# Revit family: IS_Concept_Multiproduct_BIM_GB_E0321;E0322;E0323;E0324
name_source: partatom
category: Casework
revit_build: Autodesk Revit 2015 (Build: 20140606_1530(x64)
units: mm (PartAtom-declared; Revit-internal decimal feet)

## types (8) — shared parameters
2Doors = Yes
Accessories = www.idealspec.co.uk
AreaUnits = millimeters
Assembly Code = C1030200
AssetType = Fixed
BREEAM = No
Brand = Ideal Standard
CodePerformance = FSC
ConnectionType = Plumbing
Default Elevation = 2000 mm  [stored 6.56168 ft]
DurationUnit = year
ECA = No
ExpectedLife = 30
IfcExportAs = IfcFurnitureType
IfcExportType = Bathroom cabinets
InstallationInstructions = www.idealspec.co.uk/resources.html
LinearUnits = millimeters
Manufacturer = Ideal Standard (UK) Ltd
ManufacturerURL = www.idealspec.co.uk
MetalMtl = ISI_IdealStandard_Furniture_Metal_Chrome_Render
MirrorMtl = ISI_IdealStandard_Furniture_Mirror_Render
NBSDescription = Bathroom integrated furniture
NBSReference = 45-35-72/320
NominalDepth = 170 mm  [stored 0.557743 ft]
NominalHeight = 700 mm  [stored 2.29659 ft]
NominalLength = 170 mm  [stored 0.557743 ft]
Shape = Rectangular
Space = Internal
SpareParts = www.fastpart-spares.co.uk
TMV3 = No
URL = www.idealspec.co.uk
Uniclass2 = Pr_40_30_78_03
Uniclass2015Code = Pr_40_30_78_03
Uniclass2015Description = Bathroom cabinets
Uniclass2015Reference = Pr_40_30_78_03
Uniclass2015Title = Bathroom cabinets
Uniclass2015Version = Products v1.1
Version = 1
VolumeUnits = Litres
WRAS = No
WarrantyDescription = Manufacturers Warranty
WarrantyDurationParts = 5
WarrantyDurationUnit = year
WaterEfficientProduct = No
zero-valued in all types: Cost

## per-type parameters (varying)
| type | BIMObjectName | BarCode | Color | Description | DoorC1 | DoorC2 | DoorD | Features | Finish | LaminateMtl | Model | ModelNumber | ModelReference | Name | NettWeight | NominalWidth | ProductInformation | Size |
| E0336KP - Concept Space 1300 mm Mirror cabinet - Inox | ISI_IdealStandard_Furniture_ConceptSpace_E0336KP | 5017830452188 | Aluminium Effect | Concept Space 1300 mm mirror cabinet, Aluminium Effect | 398 mm  [stored 1.30577 ft] | 398 mm  [stored 1.30577 ft] | 498 mm  [stored 1.63386 ft] | 1300 mm mirror cabinet, Aluminium Effect | Aluminium Effect | ISI_IdealStandard_Furniture_Metal_Aluminium_KP_Render | E0324KP | E0324KP | Concept Space 1300 mm mirror cabinet, Aluminium Effect | Furniture_ConceptSpace_E0336KP_IdealStandard | 36 Kg | 1300 mm  [stored 4.26509 ft] | www.idealspec.co.uk/assets/datasheet/E0336KP | 700 x 170 x 1300 mm |
| E0335KP - Concept Space 1000 mm Mirror cabinet - Inox | ISI_IdealStandard_Furniture_ConceptSpace_E0335KP | 5017830452164 | Aluminium Effect | Concept Space 1000 mm mirror cabinet, Aluminium Effect | 298 mm  [stored 0.97769 ft] | 298 mm  [stored 0.97769 ft] | 398 mm  [stored 1.30577 ft] | 1000 mm mirror cabinet, Aluminium Effect | Aluminium Effect | ISI_IdealStandard_Furniture_Metal_Aluminium_KP_Render | E0323KP | E0323KP | Concept Space 1000 mm mirror cabinet, Aluminium Effect | Furniture_ConceptSpace_E0335KP_IdealStandard | 30 Kg | 1000 mm  [stored 3.28084 ft] | www.idealspec.co.uk/assets/datasheet/E0335KP | 700 x 170 x 1000 mm |
| E0334WG - Concept Space 800 mm Mirror cabinet - White Gloss | ISI_IdealStandard_Furniture_ConceptSpace_E0334WG | 5017830452157 | Gloss White | Concept Space 800 mm mirror cabinet, Gloss White | 198 mm  [stored 0.649606 ft] | 198 mm  [stored 0.649606 ft] | 398 mm  [stored 1.30577 ft] | 800 mm mirror cabinet, Gloss White | Gloss White | ISI_IdealStandard_Furniture_Laminate_White_WG_Render | E0322WG | E0322WG | Concept Space 800 mm mirror cabinet, Gloss White | Furniture_ConceptSpace_E0334WG_IdealStandard | 24 Kg | 800 mm  [stored 2.62467 ft] | www.idealspec.co.uk/assets/datasheet/E0334WG | 700 x 170 x 800 mm |
| E0336WG - Concept Space 1300 mm Mirror cabinet - White Gloss | ISI_IdealStandard_Furniture_ConceptSpace_E0336WG | 5017830452195 | Gloss White | Concept Space 1300 mm mirror cabinet, Gloss White | 398 mm  [stored 1.30577 ft] | 398 mm  [stored 1.30577 ft] | 498 mm  [stored 1.63386 ft] | 1300 mm mirror cabinet, Gloss White | Gloss White | ISI_IdealStandard_Furniture_Laminate_White_WG_Render | E0324WG | E0324WG | Concept Space 1300 mm mirror cabinet, Gloss White | Furniture_ConceptSpace_E0336WG_IdealStandard | 36 Kg | 1300 mm  [stored 4.26509 ft] | www.idealspec.co.uk/assets/datasheet/E0336WG | 700 x 170 x 1300 mm |
| E0335WG - Concept Space 1000 mm Mirror cabinet - White Gloss | ISI_IdealStandard_Furniture_ConceptSpace_E0335WG | 5017830452171 | Gloss White | Concept Space 1000 mm mirror cabinet, Gloss White | 298 mm  [stored 0.97769 ft] | 298 mm  [stored 0.97769 ft] | 398 mm  [stored 1.30577 ft] | 1000 mm mirror cabinet, Gloss White | Gloss White | ISI_IdealStandard_Furniture_Laminate_White_WG_Render | E0323WG | E0323WG | Concept Space 1000 mm mirror cabinet, Gloss White | Furniture_ConceptSpace_E0335WG_IdealStandard | 30 Kg | 1000 mm  [stored 3.28084 ft] | www.idealspec.co.uk/assets/datasheet/E0335WG | 700 x 170 x 1000 mm |
| E0334KP - Concept Space 800 mm Mirror cabinet - Inox | ISI_IdealStandard_Furniture_ConceptSpace_E0334KP | 5017830452140 | Aluminium Effect | Concept Space 800 mm mirror cabinet, Aluminium Effect | 198 mm  [stored 0.649606 ft] | 198 mm  [stored 0.649606 ft] | 398 mm  [stored 1.30577 ft] | 800 mm mirror cabinet, Aluminium Effect | Aluminium Effect | ISI_IdealStandard_Furniture_Metal_Aluminium_KP_Render | E0322KP | E0322KP | Concept Space 800 mm mirror cabinet, Aluminium Effect | Furniture_ConceptSpace_E0334KP_IdealStandard | 24 Kg | 800 mm  [stored 2.62467 ft] | www.idealspec.co.uk/assets/datasheet/E0334KP | 700 x 170 x 800 mm |
| E0333KP - Concept Space 700 mm Mirror cabinet - Inox | ISI_IdealStandard_Furniture_ConceptSpace_E0333KP | 5017830452126 | Aluminium Effect | Concept Space 700 mm mirror cabinet, Aluminium Effect | 148 mm  [stored 0.485564 ft] | 148 mm  [stored 0.485564 ft] | 398 mm  [stored 1.30577 ft] | 700 mm mirror cabinet, Aluminium Effect | Aluminium Effect | ISI_IdealStandard_Furniture_Metal_Aluminium_KP_Render | E0321KP | E0321KP | Concept Space 700 mm mirror cabinet, Aluminium Effect | Furniture_ConceptSpace_E0333KP_IdealStandard | 22.5 Kg | 700 mm  [stored 2.29659 ft] | www.idealspec.co.uk/assets/datasheet/E0333KP | 700 x 170 x 700 mm |
| E0333WG - Concept Space 700 mm Mirror cabinet - White Gloss | ISI_IdealStandard_Furniture_ConceptSpace_E0333WG | 5017830452133 | Gloss White | Concept Space 700 mm mirror cabinet, Gloss White | 148 mm  [stored 0.485564 ft] | 148 mm  [stored 0.485564 ft] | 398 mm  [stored 1.30577 ft] | 700 mm mirror cabinet, Gloss White | Gloss White | ISI_IdealStandard_Furniture_Laminate_White_WG_Render | E0321WG | E0321WG | Concept Space 700 mm mirror cabinet, Gloss White | Furniture_ConceptSpace_E0333WG_IdealStandard | 22.5 Kg | 700 mm  [stored 2.29659 ft] | www.idealspec.co.uk/assets/datasheet/E0333WG | 700 x 170 x 700 mm |

note: [stored X ft] marks values corroborated as IEEE doubles in the binary element streams (Revit-internal decimal feet)

## geometry (parser evidence)
native form markers: Blend x2, Sweep x1
no freeform markers — native parametric forms only
